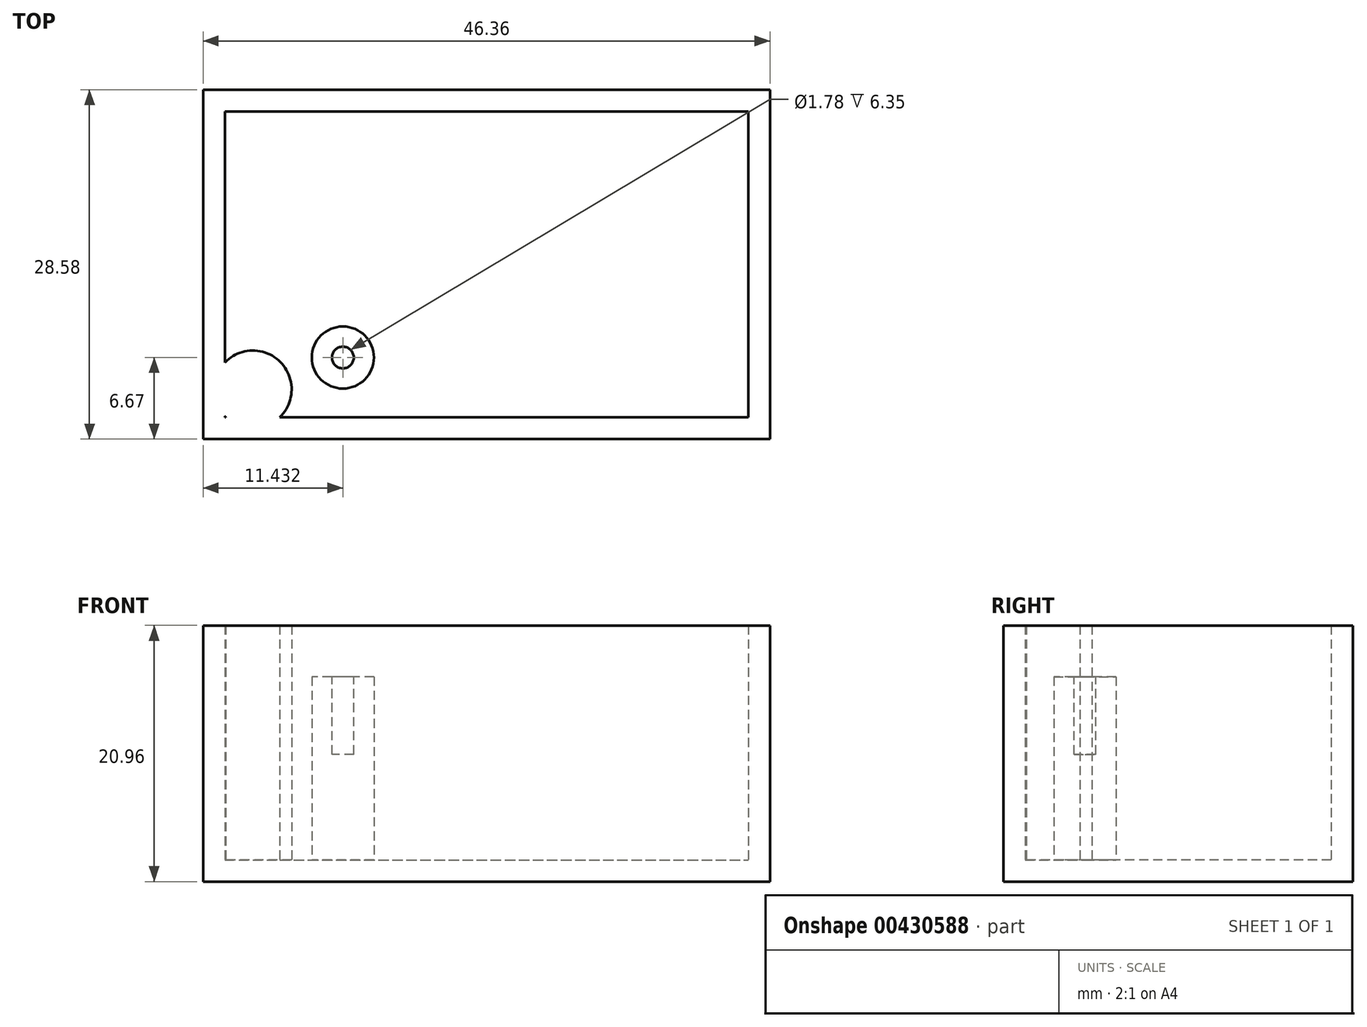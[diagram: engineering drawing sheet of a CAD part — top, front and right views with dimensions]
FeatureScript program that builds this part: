
annotation { "Feature Type Name" : "Feature", "Feature Type Description" : "" }
export const myFeature = defineFeature(function(context is Context, id is Id, definition is map)
    precondition{}
    {
        {
            var Q0;
            Q0=qCreatedBy(makeId("Top.planeOp"),FACE);
            var sketch = newSketch(context, id + "F0", { "sketchPlane" : qUnion([Q0])});
            skLineSegment(sketch, "E0.bottom", {"start": v(-23.18, 14.29) * mm, "end": v(23.18, 14.29) * mm});
            skLineSegment(sketch, "E0.top", {"start": v(-23.18, -14.29) * mm, "end": v(23.18, -14.29) * mm});
            skLineSegment(sketch, "E0.left", {"start": v(-23.18, 14.29) * mm, "end": v(-23.18, -14.29) * mm});
            skLineSegment(sketch, "E0.right", {"start": v(23.18, 14.29) * mm, "end": v(23.18, -14.29) * mm});
            skSolve(sketch);
        }
        {
            var Q0;
            Q0 = qSketchRegion(id + "F0", true);
            extrude(context, id + "F1", {"entities" : qUnion([Q0]), "depth" : 20.95 * mm});
        }
        {
            var Q0;
            Q0=makeQuery(id+"F1.opExtrude","CAP_FACE",FACE,{"disambiguationData":[OSD([sQuery(id+"F0.wireOp",EDGE,"E0.bottom"),sQuery(id+"F0.wireOp",EDGE,"E0.top"),sQuery(id+"F0.wireOp",EDGE,"E0.left"),sQuery(id+"F0.wireOp",EDGE,"E0.right")])],"isStart":false});
            shell(context, id + "F2", {"entities" : qUnion([Q0]), "thickness" : 1.78 * mm});
        }
        {
            var Q0;
            Q0=makeQuery(id+"F2.opShell","OFFSET_FACE",FACE,{"disambiguationData":[OSD([sQuery(id+"F0.wireOp",EDGE,"E0.bottom"),sQuery(id+"F0.wireOp",EDGE,"E0.top"),sQuery(id+"F0.wireOp",EDGE,"E0.left"),sQuery(id+"F0.wireOp",EDGE,"E0.right")])]});
            var sketch = newSketch(context, id + "F3", { "sketchPlane" : qUnion([Q0])});
            skCircle(sketch, "E1", {"center": v(-11.75, -7.62) * mm, "radius": 2.54 * mm});
            skSolve(sketch);
        }
        {
            var Q0;
            Q0 = qSketchRegion(id + "F3", true);
            extrude(context, id + "F4", {"entities" : qUnion([Q0]), "operationType" : NewBodyOperationType.ADD, "depth" : 15 * mm});
        }
        {
            var Q0;
            Q0=makeQuery(id+"F4.opExtrude","CAP_FACE",FACE,{"disambiguationData":[OSD([sQuery(id+"F3.wireOp",EDGE,"E1")])],"isStart":false});
            var sketch = newSketch(context, id + "F5", { "sketchPlane" : qUnion([Q0])});
            skPoint(sketch, "E2", {"position": v(-11.75, -7.62) * mm});
            skCircle(sketch, "E3", {"center": v(-11.75, -7.62) * mm, "radius": 0.89 * mm});
            skSolve(sketch);
        }
        {
            var Q0;
            Q0 = qSketchRegion(id + "F5", true);
            extrude(context, id + "F6", {"entities" : qUnion([Q0]), "operationType" : NewBodyOperationType.REMOVE, "oppositeDirection" : true, "depth" : 6.35 * mm});
        }
        {
            var Q0;
            Q0=makeQuery(id+"F2.opShell","OFFSET_FACE",FACE,{"disambiguationData":[OSD([sQuery(id+"F0.wireOp",EDGE,"E0.bottom"),sQuery(id+"F0.wireOp",EDGE,"E0.top"),sQuery(id+"F0.wireOp",EDGE,"E0.left"),sQuery(id+"F0.wireOp",EDGE,"E0.right")])]});
            var sketch = newSketch(context, id + "F7", { "sketchPlane" : qUnion([Q0])});
            skCircle(sketch, "E4", {"center": v(-19.11, -10.22) * mm, "radius": 3.18 * mm});
            skSolve(sketch);
        }
        {
            var Q0;
            Q0 = qSketchRegion(id + "F7", true);
            var Q1;
            Q1=makeQuery(id+"F1.opExtrude","CAP_FACE",FACE,{"disambiguationData":[OSD([sQuery(id+"F0.wireOp",EDGE,"E0.bottom"),sQuery(id+"F0.wireOp",EDGE,"E0.top"),sQuery(id+"F0.wireOp",EDGE,"E0.left"),sQuery(id+"F0.wireOp",EDGE,"E0.right")])],"isStart":false});
            extrude(context, id + "F8", {"entities" : qUnion([Q0]), "operationType" : NewBodyOperationType.ADD, "endBound" : BoundingType.UP_TO_SURFACE, "endBoundEntityFace" : qUnion([Q1]), "depth" : 25.4 * mm});
        }
    });
